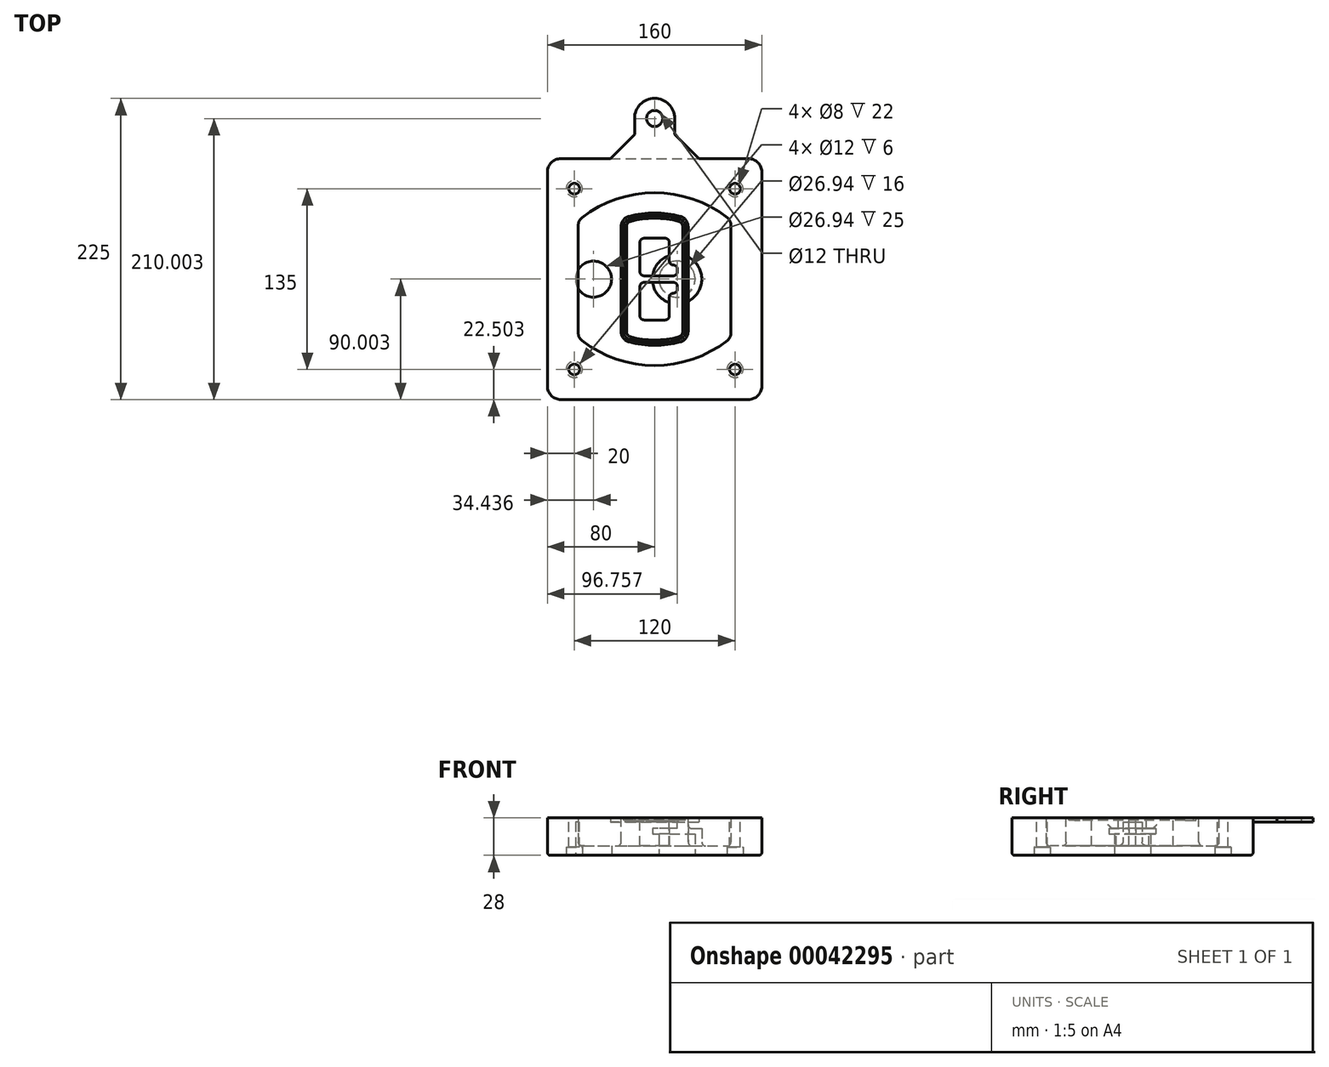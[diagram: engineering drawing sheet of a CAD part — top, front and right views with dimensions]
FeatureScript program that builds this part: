
annotation { "Feature Type Name" : "Feature", "Feature Type Description" : "" }
export const myFeature = defineFeature(function(context is Context, id is Id, definition is map)
    precondition{}
    {
        {
            var Q0;
            Q0=qCreatedBy(makeId("Top.planeOp"),FACE);
            var sketch = newSketch(context, id + "F0", { "sketchPlane" : qUnion([Q0])});
            skPoint(sketch, "E0.rect.middle", {"position": v(0, 0) * mm});
            skLineSegment(sketch, "E1.bottom", {"start": v(24.05, 28.38) * mm, "end": v(164.05, 28.38) * mm});
            skLineSegment(sketch, "E1.top", {"start": v(24.05, 208.38) * mm, "end": v(164.05, 208.38) * mm});
            skLineSegment(sketch, "E1.left", {"start": v(14.05, 38.38) * mm, "end": v(14.05, 198.38) * mm});
            skLineSegment(sketch, "E1.right", {"start": v(174.05, 38.38) * mm, "end": v(174.05, 198.38) * mm});
            skLineSegment(sketch, "E2", {"start": v(14.05, 208.38) * mm, "end": v(174.05, 28.38) * mm, "construction": true});
            skLineSegment(sketch, "E3", {"start": v(174.05, 208.38) * mm, "end": v(14.05, 28.38) * mm, "construction": true});
            skCircle(sketch, "E4", {"center": v(34.05, 185.88) * mm, "radius": 4 * mm});
            skCircle(sketch, "E5", {"center": v(154.05, 185.88) * mm, "radius": 4 * mm});
            skCircle(sketch, "E6", {"center": v(154.05, 50.88) * mm, "radius": 4 * mm});
            skCircle(sketch, "E7", {"center": v(34.05, 50.88) * mm, "radius": 4 * mm});
            skLineSegment(sketch, "E8", {"start": v(34.05, 185.88) * mm, "end": v(154.05, 185.88) * mm, "construction": true});
            skLineSegment(sketch, "E9", {"start": v(154.05, 185.88) * mm, "end": v(154.05, 50.88) * mm, "construction": true});
            skLineSegment(sketch, "E10", {"start": v(154.05, 50.88) * mm, "end": v(34.05, 50.88) * mm, "construction": true});
            skLineSegment(sketch, "E11", {"start": v(34.05, 50.88) * mm, "end": v(34.05, 185.88) * mm, "construction": true});
            skLineSegment(sketch, "E12", {"start": v(34.05, 158.68) * mm, "end": v(34.05, 78.09) * mm});
            skLineSegment(sketch, "E13", {"start": v(154.05, 158.68) * mm, "end": v(154.05, 78.09) * mm});
            skArc(sketch, "E14", {"start": v(150.2, 166.56) * mm, "mid": v(94.05, 185.88) * mm, "end": v(37.9, 166.56) * mm});
            skArc(sketch, "E15", {"start": v(37.9, 70.2) * mm, "mid": v(94.05, 50.88) * mm, "end": v(150.2, 70.2) * mm});
            skLineSegment(sketch, "E16", {"start": v(34.05, 118.38) * mm, "end": v(154.05, 118.38) * mm, "construction": true});
            skPoint(sketch, "E17.visualSharp", {"position": v(34.05, 73.38) * mm});
            skArc(sketch, "E17.filletArc", {"start": v(34.05, 78.09) * mm, "mid": v(35.06, 73.7) * mm, "end": v(37.9, 70.2) * mm});
            skPoint(sketch, "E18.visualSharp", {"position": v(34.05, 163.38) * mm});
            skArc(sketch, "E18.filletArc", {"start": v(37.9, 166.56) * mm, "mid": v(35.06, 163.06) * mm, "end": v(34.05, 158.68) * mm});
            skPoint(sketch, "E19.visualSharp", {"position": v(154.05, 163.38) * mm});
            skArc(sketch, "E19.filletArc", {"start": v(154.05, 158.68) * mm, "mid": v(153.04, 163.06) * mm, "end": v(150.2, 166.56) * mm});
            skPoint(sketch, "E20.visualSharp", {"position": v(154.05, 73.38) * mm});
            skArc(sketch, "E20.filletArc", {"start": v(150.2, 70.2) * mm, "mid": v(153.04, 73.7) * mm, "end": v(154.05, 78.09) * mm});
            skPoint(sketch, "E21.visualSharp", {"position": v(14.05, 208.38) * mm});
            skArc(sketch, "E21.filletArc", {"start": v(24.05, 208.38) * mm, "mid": v(16.98, 205.45) * mm, "end": v(14.05, 198.38) * mm});
            skPoint(sketch, "E22.visualSharp", {"position": v(174.05, 208.38) * mm});
            skArc(sketch, "E22.filletArc", {"start": v(174.05, 198.38) * mm, "mid": v(171.12, 205.45) * mm, "end": v(164.05, 208.38) * mm});
            skPoint(sketch, "E23.visualSharp", {"position": v(174.05, 28.38) * mm});
            skArc(sketch, "E23.filletArc", {"start": v(164.05, 28.38) * mm, "mid": v(171.12, 31.31) * mm, "end": v(174.05, 38.38) * mm});
            skPoint(sketch, "E24.visualSharp", {"position": v(14.05, 28.38) * mm});
            skArc(sketch, "E24.filletArc", {"start": v(14.05, 38.38) * mm, "mid": v(16.98, 31.31) * mm, "end": v(24.05, 28.38) * mm});
            skArc(sketch, "E25.0", {"start": v(151.05, 158.68) * mm, "mid": v(150.34, 161.75) * mm, "end": v(148.36, 164.2) * mm});
            skLineSegment(sketch, "E25.1", {"start": v(151.05, 158.68) * mm, "end": v(151.05, 78.09) * mm});
            skArc(sketch, "E25.2", {"start": v(148.36, 72.57) * mm, "mid": v(150.34, 75.02) * mm, "end": v(151.05, 78.09) * mm});
            skArc(sketch, "E25.3", {"start": v(39.74, 72.57) * mm, "mid": v(94.05, 53.88) * mm, "end": v(148.36, 72.57) * mm});
            skArc(sketch, "E25.4", {"start": v(37.05, 78.09) * mm, "mid": v(37.76, 75.02) * mm, "end": v(39.74, 72.57) * mm});
            skArc(sketch, "E25.5", {"start": v(148.36, 164.2) * mm, "mid": v(94.05, 182.88) * mm, "end": v(39.74, 164.2) * mm});
            skLineSegment(sketch, "E25.6", {"start": v(37.05, 158.68) * mm, "end": v(37.05, 78.09) * mm});
            skArc(sketch, "E25.7", {"start": v(39.74, 164.2) * mm, "mid": v(37.76, 161.75) * mm, "end": v(37.05, 158.68) * mm});
            skArc(sketch, "E26.0", {"start": v(35.43, 169.71) * mm, "mid": v(31.47, 164.82) * mm, "end": v(30.05, 158.68) * mm});
            skArc(sketch, "E26.1", {"start": v(152.67, 169.71) * mm, "mid": v(94.05, 189.88) * mm, "end": v(35.43, 169.71) * mm});
            skArc(sketch, "E26.2", {"start": v(158.05, 158.68) * mm, "mid": v(156.63, 164.82) * mm, "end": v(152.67, 169.71) * mm});
            skLineSegment(sketch, "E26.3", {"start": v(158.05, 158.68) * mm, "end": v(158.05, 78.09) * mm});
            skArc(sketch, "E26.4", {"start": v(152.67, 67.05) * mm, "mid": v(156.63, 71.95) * mm, "end": v(158.05, 78.09) * mm});
            skLineSegment(sketch, "E26.5", {"start": v(30.05, 158.68) * mm, "end": v(30.05, 78.09) * mm});
            skArc(sketch, "E26.6", {"start": v(35.43, 67.05) * mm, "mid": v(94.05, 46.88) * mm, "end": v(152.67, 67.05) * mm});
            skArc(sketch, "E26.7", {"start": v(30.05, 78.09) * mm, "mid": v(31.47, 71.95) * mm, "end": v(35.43, 67.05) * mm});
            skSolve(sketch);
        }
        {
            var Q0;
            Q0=makeQuery(id+"F0.imprint","IMPRINT",FACE,{"disambiguationData":[TD([[makeQuery(id+"F0.imprint","IMPRINT",EDGE,{"derivedFrom":sQuery(id+"F0.wireOp",EDGE,"E1.bottom")}),1.0]])]});
            var Q1;
            Q1=makeQuery(id+"F0.imprint","IMPRINT",FACE,{"disambiguationData":[TD([[makeQuery(id+"F0.imprint","IMPRINT",EDGE,{"derivedFrom":sQuery(id+"F0.wireOp",EDGE,"E12")}),1.0]])]});
            var Q2;
            Q2=makeQuery(id+"F0.imprint","IMPRINT",FACE,{"disambiguationData":[TD([[makeQuery(id+"F0.imprint","IMPRINT",EDGE,{"derivedFrom":sQuery(id+"F0.wireOp",EDGE,"E25.0")}),1.0]])]});
            var Q3;
            Q3=makeQuery(id+"F0.imprint","IMPRINT",FACE,{"disambiguationData":[TD([[makeQuery(id+"F0.imprint","IMPRINT",EDGE,{"derivedFrom":sQuery(id+"F0.wireOp",EDGE,"E12")}),-1.0]])]});
            extrude(context, id + "F1", {"entities" : qUnion([Q0, Q1, Q2, Q3]), "oppositeDirection" : true, "depth" : 25 * mm});
        }
        {
            var Q0;
            Q0=makeQuery(id+"F0.imprint","IMPRINT",FACE,{"disambiguationData":[TD([[makeQuery(id+"F0.imprint","IMPRINT",EDGE,{"derivedFrom":sQuery(id+"F0.wireOp",EDGE,"E12")}),1.0]])]});
            extrude(context, id + "F2", {"entities" : qUnion([Q0]), "operationType" : NewBodyOperationType.ADD, "depth" : 3 * mm});
        }
        {
            var Q0;
            Q0=makeQuery(id+"F0.imprint","IMPRINT",FACE,{"disambiguationData":[TD([[makeQuery(id+"F0.imprint","IMPRINT",EDGE,{"derivedFrom":sQuery(id+"F0.wireOp",EDGE,"E25.0")}),1.0]])]});
            extrude(context, id + "F3", {"entities" : qUnion([Q0]), "operationType" : NewBodyOperationType.REMOVE, "oppositeDirection" : true, "depth" : 18 * mm});
        }
        {
            var Q0;
            Q0=makeQuery(id+"F2.opExtrude","CAP_FACE",FACE,{"disambiguationData":[OSD([sQuery(id+"F0.wireOp",EDGE,"E12"),sQuery(id+"F0.wireOp",EDGE,"E13"),sQuery(id+"F0.wireOp",EDGE,"E14"),sQuery(id+"F0.wireOp",EDGE,"E15"),sQuery(id+"F0.wireOp",EDGE,"E17.filletArc"),sQuery(id+"F0.wireOp",EDGE,"E18.filletArc"),sQuery(id+"F0.wireOp",EDGE,"E19.filletArc"),sQuery(id+"F0.wireOp",EDGE,"E20.filletArc"),sQuery(id+"F0.wireOp",EDGE,"E25.0"),sQuery(id+"F0.wireOp",EDGE,"E25.1"),sQuery(id+"F0.wireOp",EDGE,"E25.2"),sQuery(id+"F0.wireOp",EDGE,"E25.3"),sQuery(id+"F0.wireOp",EDGE,"E25.4"),sQuery(id+"F0.wireOp",EDGE,"E25.5"),sQuery(id+"F0.wireOp",EDGE,"E25.6"),sQuery(id+"F0.wireOp",EDGE,"E25.7")])],"isStart":false});
            var sketch = newSketch(context, id + "F4", { "sketchPlane" : qUnion([Q0])});
            skArc(sketch, "E27.0", {"start": v(74.97, 71.41) * mm, "mid": v(94.05, 68.88) * mm, "end": v(113.13, 71.41) * mm});
            skArc(sketch, "E28.0", {"start": v(113.13, 165.35) * mm, "mid": v(94.05, 167.88) * mm, "end": v(74.97, 165.35) * mm});
            skLineSegment(sketch, "E29", {"start": v(69.05, 157.63) * mm, "end": v(69.05, 79.14) * mm});
            skLineSegment(sketch, "E30", {"start": v(119.05, 157.63) * mm, "end": v(119.05, 79.14) * mm});
            skLineSegment(sketch, "E31", {"start": v(69.05, 163.48) * mm, "end": v(119.05, 163.48) * mm, "construction": true});
            skLineSegment(sketch, "E32", {"start": v(69.05, 73.28) * mm, "end": v(119.05, 73.28) * mm, "construction": true});
            skPoint(sketch, "E33.visualSharp", {"position": v(69.05, 163.48) * mm});
            skArc(sketch, "E33.filletArc", {"start": v(74.97, 165.35) * mm, "mid": v(70.7, 162.5) * mm, "end": v(69.05, 157.63) * mm});
            skPoint(sketch, "E34.visualSharp", {"position": v(119.05, 163.48) * mm});
            skArc(sketch, "E34.filletArc", {"start": v(119.05, 157.63) * mm, "mid": v(117.4, 162.5) * mm, "end": v(113.13, 165.35) * mm});
            skPoint(sketch, "E35.visualSharp", {"position": v(119.05, 73.28) * mm});
            skArc(sketch, "E35.filletArc", {"start": v(113.13, 71.41) * mm, "mid": v(117.4, 74.27) * mm, "end": v(119.05, 79.14) * mm});
            skPoint(sketch, "E36.visualSharp", {"position": v(69.05, 73.28) * mm});
            skArc(sketch, "E36.filletArc", {"start": v(69.05, 79.14) * mm, "mid": v(70.7, 74.27) * mm, "end": v(74.97, 71.41) * mm});
            skArc(sketch, "E37.0", {"start": v(148.36, 164.2) * mm, "mid": v(94.05, 182.88) * mm, "end": v(39.74, 164.2) * mm});
            skArc(sketch, "E37.1", {"start": v(39.74, 164.2) * mm, "mid": v(37.76, 161.75) * mm, "end": v(37.05, 158.68) * mm});
            skLineSegment(sketch, "E37.2", {"start": v(37.05, 158.68) * mm, "end": v(37.05, 78.09) * mm});
            skArc(sketch, "E37.3", {"start": v(37.05, 78.09) * mm, "mid": v(37.76, 75.02) * mm, "end": v(39.74, 72.57) * mm});
            skArc(sketch, "E37.4", {"start": v(39.74, 72.57) * mm, "mid": v(94.05, 53.88) * mm, "end": v(148.36, 72.57) * mm});
            skArc(sketch, "E37.5", {"start": v(148.36, 72.57) * mm, "mid": v(150.34, 75.02) * mm, "end": v(151.05, 78.09) * mm});
            skLineSegment(sketch, "E37.6", {"start": v(151.05, 158.68) * mm, "end": v(151.05, 78.09) * mm});
            skArc(sketch, "E37.7", {"start": v(151.05, 158.68) * mm, "mid": v(150.34, 161.75) * mm, "end": v(148.36, 164.2) * mm});
            skLineSegment(sketch, "E38.0", {"start": v(117.05, 157.63) * mm, "end": v(117.05, 79.14) * mm});
            skArc(sketch, "E38.1", {"start": v(112.61, 73.34) * mm, "mid": v(115.81, 75.49) * mm, "end": v(117.05, 79.14) * mm});
            skArc(sketch, "E38.2", {"start": v(75.49, 73.34) * mm, "mid": v(94.05, 70.88) * mm, "end": v(112.61, 73.34) * mm});
            skArc(sketch, "E38.3", {"start": v(71.05, 79.14) * mm, "mid": v(72.29, 75.49) * mm, "end": v(75.49, 73.34) * mm});
            skLineSegment(sketch, "E38.4", {"start": v(71.05, 157.63) * mm, "end": v(71.05, 79.14) * mm});
            skArc(sketch, "E38.5", {"start": v(117.05, 157.63) * mm, "mid": v(115.81, 161.28) * mm, "end": v(112.61, 163.42) * mm});
            skArc(sketch, "E38.6", {"start": v(75.49, 163.42) * mm, "mid": v(72.29, 161.28) * mm, "end": v(71.05, 157.63) * mm});
            skArc(sketch, "E38.7", {"start": v(112.61, 163.42) * mm, "mid": v(94.05, 165.88) * mm, "end": v(75.49, 163.42) * mm});
            skArc(sketch, "E39.0", {"start": v(115.05, 157.63) * mm, "mid": v(114.23, 160.06) * mm, "end": v(112.1, 161.5) * mm});
            skLineSegment(sketch, "E39.1", {"start": v(115.05, 157.63) * mm, "end": v(115.05, 79.14) * mm});
            skArc(sketch, "E39.2", {"start": v(112.1, 75.27) * mm, "mid": v(114.23, 76.7) * mm, "end": v(115.05, 79.14) * mm});
            skArc(sketch, "E39.3", {"start": v(76, 75.27) * mm, "mid": v(94.05, 72.88) * mm, "end": v(112.1, 75.27) * mm});
            skArc(sketch, "E39.4", {"start": v(73.05, 79.14) * mm, "mid": v(73.87, 76.7) * mm, "end": v(76, 75.27) * mm});
            skArc(sketch, "E39.5", {"start": v(112.1, 161.5) * mm, "mid": v(94.05, 163.88) * mm, "end": v(76, 161.5) * mm});
            skLineSegment(sketch, "E39.6", {"start": v(73.05, 157.63) * mm, "end": v(73.05, 79.14) * mm});
            skArc(sketch, "E39.7", {"start": v(76, 161.5) * mm, "mid": v(73.87, 160.06) * mm, "end": v(73.05, 157.63) * mm});
            skLineSegment(sketch, "E40", {"start": v(69.05, 118.38) * mm, "end": v(119.05, 118.38) * mm, "construction": true});
            skLineSegment(sketch, "E41", {"start": v(83.05, 123.88) * mm, "end": v(83.05, 145.88) * mm});
            skLineSegment(sketch, "E42", {"start": v(86.05, 148.88) * mm, "end": v(102.05, 148.88) * mm});
            skLineSegment(sketch, "E43", {"start": v(105.05, 145.88) * mm, "end": v(105.05, 131.88) * mm});
            skLineSegment(sketch, "E44", {"start": v(108.05, 128.88) * mm, "end": v(108.05, 128.88) * mm});
            skLineSegment(sketch, "E45", {"start": v(111.05, 125.88) * mm, "end": v(111.05, 123.88) * mm});
            skLineSegment(sketch, "E46", {"start": v(108.05, 120.88) * mm, "end": v(86.05, 120.88) * mm});
            skPoint(sketch, "E47.visualSharp", {"position": v(83.05, 148.88) * mm});
            skArc(sketch, "E47.filletArc", {"start": v(86.05, 148.88) * mm, "mid": v(83.93, 148) * mm, "end": v(83.05, 145.88) * mm});
            skPoint(sketch, "E48.visualSharp", {"position": v(105.05, 148.88) * mm});
            skArc(sketch, "E48.filletArc", {"start": v(105.05, 145.88) * mm, "mid": v(104.17, 148) * mm, "end": v(102.05, 148.88) * mm});
            skPoint(sketch, "E49.visualSharp", {"position": v(105.05, 128.88) * mm});
            skArc(sketch, "E49.filletArc", {"start": v(105.05, 131.88) * mm, "mid": v(105.93, 129.76) * mm, "end": v(108.05, 128.88) * mm});
            skPoint(sketch, "E50.visualSharp", {"position": v(111.05, 128.88) * mm});
            skArc(sketch, "E50.filletArc", {"start": v(111.05, 125.88) * mm, "mid": v(110.17, 128) * mm, "end": v(108.05, 128.88) * mm});
            skPoint(sketch, "E51.visualSharp", {"position": v(111.05, 120.88) * mm});
            skArc(sketch, "E51.filletArc", {"start": v(108.05, 120.88) * mm, "mid": v(110.17, 121.76) * mm, "end": v(111.05, 123.88) * mm});
            skPoint(sketch, "E52.visualSharp", {"position": v(83.05, 120.88) * mm});
            skArc(sketch, "E52.filletArc", {"start": v(83.05, 123.88) * mm, "mid": v(83.93, 121.76) * mm, "end": v(86.05, 120.88) * mm});
            skLineSegment(sketch, "E53.0.MirrorCS", {"start": v(108.05, 115.88) * mm, "end": v(86.05, 115.88) * mm});
            skArc(sketch, "E54.0.MirrorCS", {"start": v(83.05, 112.88) * mm, "mid": v(83.93, 115) * mm, "end": v(86.05, 115.88) * mm});
            skLineSegment(sketch, "E55.0.MirrorCS", {"start": v(83.05, 112.88) * mm, "end": v(83.05, 90.88) * mm});
            skArc(sketch, "E56.0.MirrorCS", {"start": v(86.05, 87.88) * mm, "mid": v(83.93, 88.76) * mm, "end": v(83.05, 90.88) * mm});
            skLineSegment(sketch, "E57.0.MirrorCS", {"start": v(86.05, 87.88) * mm, "end": v(102.05, 87.88) * mm});
            skArc(sketch, "E58.0.MirrorCS", {"start": v(105.05, 90.88) * mm, "mid": v(104.17, 88.76) * mm, "end": v(102.05, 87.88) * mm});
            skLineSegment(sketch, "E59.0.MirrorCS", {"start": v(105.05, 90.88) * mm, "end": v(105.05, 104.88) * mm});
            skArc(sketch, "E60.0.MirrorCS", {"start": v(105.05, 104.88) * mm, "mid": v(105.93, 107) * mm, "end": v(108.05, 107.88) * mm});
            skArc(sketch, "E61.0.MirrorCS", {"start": v(111.05, 110.88) * mm, "mid": v(110.17, 108.76) * mm, "end": v(108.05, 107.88) * mm});
            skLineSegment(sketch, "E62.0.MirrorCS", {"start": v(111.05, 110.88) * mm, "end": v(111.05, 112.88) * mm});
            skArc(sketch, "E63.0.MirrorCS", {"start": v(108.05, 115.88) * mm, "mid": v(110.17, 115) * mm, "end": v(111.05, 112.88) * mm});
            skSolve(sketch);
        }
        {
            var Q0;
            Q0=makeQuery(id+"F4.imprint","IMPRINT",FACE,{"disambiguationData":[TD([[makeQuery(id+"F4.imprint","IMPRINT",EDGE,{"derivedFrom":sQuery(id+"F4.wireOp",EDGE,"E27.0")}),1.0]])]});
            var Q1;
            Q1=makeQuery(id+"F4.imprint","IMPRINT",FACE,{"disambiguationData":[TD([[makeQuery(id+"F4.imprint","IMPRINT",EDGE,{"derivedFrom":sQuery(id+"F4.wireOp",EDGE,"E38.0")}),-1.0]])]});
            var Q2;
            Q2=makeQuery(id+"F4.imprint","IMPRINT",FACE,{"disambiguationData":[TD([[makeQuery(id+"F4.imprint","IMPRINT",EDGE,{"derivedFrom":sQuery(id+"F4.wireOp",EDGE,"E39.0")}),1.0]])]});
            extrude(context, id + "F5", {"entities" : qUnion([Q0, Q1, Q2]), "operationType" : NewBodyOperationType.ADD, "endBound" : BoundingType.UP_TO_NEXT, "oppositeDirection" : true, "depth" : 25 * mm});
        }
        {
            var Q0;
            Q0=makeQuery(id+"F4.imprint","IMPRINT",FACE,{"disambiguationData":[TD([[makeQuery(id+"F4.imprint","IMPRINT",EDGE,{"derivedFrom":sQuery(id+"F4.wireOp",EDGE,"E38.0")}),-1.0]])]});
            extrude(context, id + "F6", {"entities" : qUnion([Q0]), "operationType" : NewBodyOperationType.REMOVE, "oppositeDirection" : true, "depth" : 2 * mm});
        }
        {
            var Q0;
            Q0=makeQuery(id+"F1.opExtrude","CAP_FACE",FACE,{"disambiguationData":[OSD([sQuery(id+"F0.wireOp",EDGE,"E1.bottom"),sQuery(id+"F0.wireOp",EDGE,"E1.top"),sQuery(id+"F0.wireOp",EDGE,"E1.left"),sQuery(id+"F0.wireOp",EDGE,"E1.right"),sQuery(id+"F0.wireOp",EDGE,"E4"),sQuery(id+"F0.wireOp",EDGE,"E5"),sQuery(id+"F0.wireOp",EDGE,"E6"),sQuery(id+"F0.wireOp",EDGE,"E7"),sQuery(id+"F0.wireOp",EDGE,"E21.filletArc"),sQuery(id+"F0.wireOp",EDGE,"E22.filletArc"),sQuery(id+"F0.wireOp",EDGE,"E23.filletArc"),sQuery(id+"F0.wireOp",EDGE,"E24.filletArc")])],"isStart":false});
            var sketch = newSketch(context, id + "F7", { "sketchPlane" : qUnion([Q0])});
            skCircle(sketch, "E64", {"center": v(110.8, -118.38) * mm, "radius": 13.47 * mm});
            skCircle(sketch, "E65", {"center": v(48.49, -118.38) * mm, "radius": 13.47 * mm});
            skLineSegment(sketch, "E66", {"start": v(174.05, -118.38) * mm, "end": v(14.05, -118.38) * mm});
            skCircle(sketch, "E67", {"center": v(110.8, -118.38) * mm, "radius": 18.47 * mm});
            skCircle(sketch, "E68", {"center": v(154.05, -185.88) * mm, "radius": 6 * mm});
            skCircle(sketch, "E69", {"center": v(34.05, -185.88) * mm, "radius": 6 * mm});
            skCircle(sketch, "E70", {"center": v(34.05, -50.88) * mm, "radius": 6 * mm});
            skCircle(sketch, "E71", {"center": v(154.05, -50.88) * mm, "radius": 6 * mm});
            skSolve(sketch);
        }
        {
            var Q0;
            {var subQ1=sQuery(id+"F7.wireOp",EDGE,"E66");var subQ4=sQuery(id+"F7.wireOp",EDGE,"E64");var subQ6=makeQuery(id+"F7.imprint","INTERSECT",VERTEX,{"disambiguationData":[OD(0.0)],"derivedFrom":[subQ4,subQ1]});Q0=makeQuery(id+"F7.imprint","IMPRINT",FACE,{"disambiguationData":[TD([[makeQuery(id+"F7.imprint","IMPRINT",EDGE,{"disambiguationData":[TD([[subQ6,-1.0]])],"derivedFrom":subQ4}),-1.0]])]});}
            var Q1;
            {var subQ0=sQuery(id+"F7.wireOp",EDGE,"E66");var subQ1=sQuery(id+"F7.wireOp",EDGE,"E64");var subQ3=makeQuery(id+"F7.imprint","INTERSECT",VERTEX,{"disambiguationData":[OD(0.0)],"derivedFrom":[subQ1,subQ0]});Q1=makeQuery(id+"F7.imprint","IMPRINT",FACE,{"disambiguationData":[TD([[makeQuery(id+"F7.imprint","IMPRINT",EDGE,{"disambiguationData":[TD([[subQ3,-1.0]])],"derivedFrom":subQ1}),1.0]])]});}
            var Q2;
            {var subQ0=sQuery(id+"F7.wireOp",EDGE,"E66");var subQ1=sQuery(id+"F7.wireOp",EDGE,"E64");var subQ3=makeQuery(id+"F7.imprint","INTERSECT",VERTEX,{"disambiguationData":[OD(0.0)],"derivedFrom":[subQ1,subQ0]});Q2=makeQuery(id+"F7.imprint","IMPRINT",FACE,{"disambiguationData":[TD([[makeQuery(id+"F7.imprint","IMPRINT",EDGE,{"disambiguationData":[TD([[subQ3,1.0]])],"derivedFrom":subQ1}),1.0]])]});}
            var Q3;
            {var subQ1=sQuery(id+"F7.wireOp",EDGE,"E66");var subQ4=sQuery(id+"F7.wireOp",EDGE,"E64");var subQ6=makeQuery(id+"F7.imprint","INTERSECT",VERTEX,{"disambiguationData":[OD(0.0)],"derivedFrom":[subQ4,subQ1]});Q3=makeQuery(id+"F7.imprint","IMPRINT",FACE,{"disambiguationData":[TD([[makeQuery(id+"F7.imprint","IMPRINT",EDGE,{"disambiguationData":[TD([[subQ6,1.0]])],"derivedFrom":subQ4}),-1.0]])]});}
            extrude(context, id + "F8", {"entities" : qUnion([Q0, Q1, Q2, Q3]), "operationType" : NewBodyOperationType.ADD, "oppositeDirection" : true, "depth" : 20 * mm});
        }
        {
            var Q0;
            {var subQ0=sQuery(id+"F7.wireOp",EDGE,"E66");var subQ1=sQuery(id+"F7.wireOp",EDGE,"E64");var subQ3=makeQuery(id+"F7.imprint","INTERSECT",VERTEX,{"disambiguationData":[OD(0.0)],"derivedFrom":[subQ1,subQ0]});Q0=makeQuery(id+"F7.imprint","IMPRINT",FACE,{"disambiguationData":[TD([[makeQuery(id+"F7.imprint","IMPRINT",EDGE,{"disambiguationData":[TD([[subQ3,-1.0]])],"derivedFrom":subQ1}),1.0]])]});}
            var Q1;
            {var subQ0=sQuery(id+"F7.wireOp",EDGE,"E66");var subQ1=sQuery(id+"F7.wireOp",EDGE,"E64");var subQ3=makeQuery(id+"F7.imprint","INTERSECT",VERTEX,{"disambiguationData":[OD(0.0)],"derivedFrom":[subQ1,subQ0]});Q1=makeQuery(id+"F7.imprint","IMPRINT",FACE,{"disambiguationData":[TD([[makeQuery(id+"F7.imprint","IMPRINT",EDGE,{"disambiguationData":[TD([[subQ3,1.0]])],"derivedFrom":subQ1}),1.0]])]});}
            extrude(context, id + "F9", {"entities" : qUnion([Q0, Q1]), "operationType" : NewBodyOperationType.REMOVE, "oppositeDirection" : true, "depth" : 16 * mm});
        }
        {
            var Q0;
            {var subQ0=sQuery(id+"F7.wireOp",EDGE,"E66");var subQ1=sQuery(id+"F7.wireOp",EDGE,"E65");var subQ3=makeQuery(id+"F7.imprint","INTERSECT",VERTEX,{"disambiguationData":[OD(0.0)],"derivedFrom":[subQ1,subQ0]});Q0=makeQuery(id+"F7.imprint","IMPRINT",FACE,{"disambiguationData":[TD([[makeQuery(id+"F7.imprint","IMPRINT",EDGE,{"disambiguationData":[TD([[subQ3,-1.0]])],"derivedFrom":subQ1}),1.0]])]});}
            var Q1;
            {var subQ0=sQuery(id+"F7.wireOp",EDGE,"E66");var subQ1=sQuery(id+"F7.wireOp",EDGE,"E65");var subQ3=makeQuery(id+"F7.imprint","INTERSECT",VERTEX,{"disambiguationData":[OD(0.0)],"derivedFrom":[subQ1,subQ0]});Q1=makeQuery(id+"F7.imprint","IMPRINT",FACE,{"disambiguationData":[TD([[makeQuery(id+"F7.imprint","IMPRINT",EDGE,{"disambiguationData":[TD([[subQ3,1.0]])],"derivedFrom":subQ1}),1.0]])]});}
            extrude(context, id + "F10", {"entities" : qUnion([Q0, Q1]), "operationType" : NewBodyOperationType.REMOVE, "oppositeDirection" : true, "depth" : 25 * mm});
        }
        {
            var Q0;
            Q0=makeQuery(id+"F7.imprint","IMPRINT",FACE,{"disambiguationData":[TD([[makeQuery(id+"F7.imprint","IMPRINT",EDGE,{"derivedFrom":sQuery(id+"F7.wireOp",EDGE,"E68")}),1.0]])]});
            var Q1;
            Q1=makeQuery(id+"F7.imprint","IMPRINT",FACE,{"disambiguationData":[TD([[makeQuery(id+"F7.imprint","IMPRINT",EDGE,{"derivedFrom":makeQuery(id+"F1.opExtrude","CAP_EDGE",EDGE,{"disambiguationData":[OSD([sQuery(id+"F0.wireOp",EDGE,"E5")])],"isStart":false})}),-1.0]])]});
            var Q2;
            Q2=makeQuery(id+"F7.imprint","IMPRINT",FACE,{"disambiguationData":[TD([[makeQuery(id+"F7.imprint","IMPRINT",EDGE,{"derivedFrom":sQuery(id+"F7.wireOp",EDGE,"E69")}),1.0]])]});
            var Q3;
            Q3=makeQuery(id+"F7.imprint","IMPRINT",FACE,{"disambiguationData":[TD([[makeQuery(id+"F7.imprint","IMPRINT",EDGE,{"derivedFrom":makeQuery(id+"F1.opExtrude","CAP_EDGE",EDGE,{"disambiguationData":[OSD([sQuery(id+"F0.wireOp",EDGE,"E4")])],"isStart":false})}),-1.0]])]});
            var Q4;
            Q4=makeQuery(id+"F7.imprint","IMPRINT",FACE,{"disambiguationData":[TD([[makeQuery(id+"F7.imprint","IMPRINT",EDGE,{"derivedFrom":sQuery(id+"F7.wireOp",EDGE,"E70")}),1.0]])]});
            var Q5;
            Q5=makeQuery(id+"F7.imprint","IMPRINT",FACE,{"disambiguationData":[TD([[makeQuery(id+"F7.imprint","IMPRINT",EDGE,{"derivedFrom":makeQuery(id+"F1.opExtrude","CAP_EDGE",EDGE,{"disambiguationData":[OSD([sQuery(id+"F0.wireOp",EDGE,"E7")])],"isStart":false})}),-1.0]])]});
            var Q6;
            Q6=makeQuery(id+"F7.imprint","IMPRINT",FACE,{"disambiguationData":[TD([[makeQuery(id+"F7.imprint","IMPRINT",EDGE,{"derivedFrom":sQuery(id+"F7.wireOp",EDGE,"E71")}),1.0]])]});
            var Q7;
            Q7=makeQuery(id+"F7.imprint","IMPRINT",FACE,{"disambiguationData":[TD([[makeQuery(id+"F7.imprint","IMPRINT",EDGE,{"derivedFrom":makeQuery(id+"F1.opExtrude","CAP_EDGE",EDGE,{"disambiguationData":[OSD([sQuery(id+"F0.wireOp",EDGE,"E6")])],"isStart":false})}),-1.0]])]});
            extrude(context, id + "F11", {"entities" : qUnion([Q0, Q1, Q2, Q3, Q4, Q5, Q6, Q7]), "operationType" : NewBodyOperationType.REMOVE, "oppositeDirection" : true, "depth" : 6 * mm});
        }
        {
            var Q0;
            Q0=makeQuery(id+"F9.boolean.opBoolean","COPY",FACE,{"derivedFrom":makeQuery(id+"F9.opExtrude","CAP_FACE",FACE,{"disambiguationData":[OSD([sQuery(id+"F7.wireOp",EDGE,"E64")])],"isStart":false})});
            var sketch = newSketch(context, id + "F12", { "sketchPlane" : qUnion([Q0])});
            skArc(sketch, "E72.0", {"start": v(105.05, -100.83) * mm, "mid": v(96.62, -106.56) * mm, "end": v(92.5, -115.88) * mm});
            skArc(sketch, "E72.1", {"start": v(92.5, -120.88) * mm, "mid": v(96.62, -130.2) * mm, "end": v(105.05, -135.93) * mm});
            skLineSegment(sketch, "E73", {"start": v(92.5, -120.88) * mm, "end": v(108.05, -120.88) * mm});
            skLineSegment(sketch, "E74.0", {"start": v(108.05, -115.88) * mm, "end": v(92.5, -115.88) * mm});
            skArc(sketch, "E74.1", {"start": v(108.05, -115.88) * mm, "mid": v(110.17, -115) * mm, "end": v(111.05, -112.88) * mm});
            skLineSegment(sketch, "E74.2", {"start": v(111.05, -110.88) * mm, "end": v(111.05, -112.88) * mm});
            skArc(sketch, "E74.3", {"start": v(111.05, -110.88) * mm, "mid": v(110.17, -108.76) * mm, "end": v(108.05, -107.88) * mm});
            skArc(sketch, "E74.4", {"start": v(105.05, -104.88) * mm, "mid": v(105.93, -107) * mm, "end": v(108.05, -107.88) * mm});
            skLineSegment(sketch, "E74.5", {"start": v(105.05, -100.83) * mm, "end": v(105.05, -104.88) * mm});
            skLineSegment(sketch, "E74.7", {"start": v(108.05, -120.88) * mm, "end": v(92.5, -120.88) * mm});
            skArc(sketch, "E74.8", {"start": v(108.05, -120.88) * mm, "mid": v(110.17, -121.76) * mm, "end": v(111.05, -123.88) * mm});
            skLineSegment(sketch, "E74.9", {"start": v(111.05, -125.88) * mm, "end": v(111.05, -123.88) * mm});
            skArc(sketch, "E74.10", {"start": v(111.05, -125.88) * mm, "mid": v(110.17, -128) * mm, "end": v(108.05, -128.88) * mm});
            skArc(sketch, "E74.11", {"start": v(105.05, -131.88) * mm, "mid": v(105.93, -129.76) * mm, "end": v(108.05, -128.88) * mm});
            skLineSegment(sketch, "E74.12", {"start": v(105.05, -135.93) * mm, "end": v(105.05, -131.88) * mm});
            skPoint(sketch, "E75.orphan", {"position": v(105.05, -145.88) * mm});
            skPoint(sketch, "E76.orphan", {"position": v(86.05, -120.88) * mm});
            skPoint(sketch, "E77.orphan", {"position": v(86.05, -115.88) * mm});
            skPoint(sketch, "E78.orphan", {"position": v(105.05, -90.88) * mm});
            skSolve(sketch);
        }
        {
            var Q0;
            {var subQ7=sQuery(id+"F12.wireOp",EDGE,"E72.0");var subQ14=sQuery(id+"F12.wireOp",EDGE,"E72.1");var subQ16=sQuery(id+"F12.wireOp",EDGE,"E74.1");var subQ18=sQuery(id+"F12.wireOp",EDGE,"E74.8");Q0=qUnion([makeQuery(id+"F12.imprint","IMPRINT",FACE,{"disambiguationData":[TD([[makeQuery(id+"F12.imprint","IMPRINT",EDGE,{"derivedFrom":subQ7}),1.0]])]}),makeQuery(id+"F12.imprint","IMPRINT",FACE,{"disambiguationData":[TD([[makeQuery(id+"F12.imprint","IMPRINT",EDGE,{"derivedFrom":subQ14}),1.0]])]}),makeQuery(id+"F12.imprint","IMPRINT",FACE,{"disambiguationData":[TD([[makeQuery(id+"F12.imprint","IMPRINT",EDGE,{"derivedFrom":subQ16}),1.0]])]}),makeQuery(id+"F12.imprint","IMPRINT",FACE,{"disambiguationData":[TD([[makeQuery(id+"F12.imprint","IMPRINT",EDGE,{"derivedFrom":subQ18}),-1.0]])]})]);}
            var Q1;
            Q1=makeQuery(id+"F5.boolean.opBoolean","SPLIT",FACE,{"disambiguationData":[TD([makeQuery(id+"F5.opExtrude","SWEPT_FACE",FACE,{"disambiguationData":[OSD([sQuery(id+"F4.wireOp",EDGE,"E41")])]})])],"derivedFrom":makeQuery(id+"F3.boolean.opBoolean","COPY",FACE,{"derivedFrom":makeQuery(id+"F3.opExtrude","CAP_FACE",FACE,{"disambiguationData":[OSD([sQuery(id+"F0.wireOp",EDGE,"E25.0"),sQuery(id+"F0.wireOp",EDGE,"E25.1"),sQuery(id+"F0.wireOp",EDGE,"E25.2"),sQuery(id+"F0.wireOp",EDGE,"E25.3"),sQuery(id+"F0.wireOp",EDGE,"E25.4"),sQuery(id+"F0.wireOp",EDGE,"E25.5"),sQuery(id+"F0.wireOp",EDGE,"E25.6"),sQuery(id+"F0.wireOp",EDGE,"E25.7")])],"isStart":false})})});
            extrude(context, id + "F13", {"entities" : qUnion([Q0]), "operationType" : NewBodyOperationType.REMOVE, "endBound" : BoundingType.UP_TO_SURFACE, "endBoundEntityFace" : qUnion([Q1]), "depth" : 25 * mm});
        }
        {
            var Q0;
            Q0=makeQuery(id+"F3.boolean.opBoolean","COPY",EDGE,{"derivedFrom":makeQuery(id+"F3.opExtrude","CAP_EDGE",EDGE,{"disambiguationData":[OSD([sQuery(id+"F0.wireOp",EDGE,"E25.6")])],"isStart":false})});
            var Q1;
            Q1=makeQuery(id+"F8.boolean.opBoolean","INTERSECT",EDGE,{"derivedFrom":[makeQuery(id+"F5.opExtrude","SWEPT_FACE",FACE,{"disambiguationData":[OSD([sQuery(id+"F4.wireOp",EDGE,"E30")])]}),makeQuery(id+"F8.opExtrude","CAP_FACE",FACE,{"disambiguationData":[OSD([sQuery(id+"F7.wireOp",EDGE,"E67")])],"isStart":false})]});
            var Q2;
            Q2=makeQuery(id+"F8.boolean.opBoolean","INTERSECT",EDGE,{"disambiguationData":[OD(1.0)],"derivedFrom":[makeQuery(id+"F5.opExtrude","SWEPT_FACE",FACE,{"disambiguationData":[OSD([sQuery(id+"F4.wireOp",EDGE,"E30")])]}),makeQuery(id+"F8.opExtrude","SWEPT_FACE",FACE,{"disambiguationData":[OSD([sQuery(id+"F7.wireOp",EDGE,"E67")])]})]});
            var Q3;
            {var subQ0=sQuery(id+"F4.wireOp",EDGE,"E30");Q3=makeQuery(id+"F8.boolean.opBoolean","SPLIT",EDGE,{"disambiguationData":[TD([makeQuery(id+"F5.opExtrude","SWEPT_FACE",FACE,{"disambiguationData":[OSD([sQuery(id+"F4.wireOp",EDGE,"E35.filletArc")])]})])],"derivedFrom":makeQuery(id+"F5.opExtrude","CAP_EDGE",EDGE,{"disambiguationData":[OSD([subQ0])],"isStart":false})});}
            var Q4;
            {var subQ0=sQuery(id+"F0.wireOp",EDGE,"E25.7");var subQ1=sQuery(id+"F0.wireOp",EDGE,"E25.1");var subQ2=sQuery(id+"F0.wireOp",EDGE,"E25.6");var subQ3=sQuery(id+"F0.wireOp",EDGE,"E25.5");var subQ4=sQuery(id+"F0.wireOp",EDGE,"E25.4");var subQ5=sQuery(id+"F0.wireOp",EDGE,"E25.0");var subQ6=sQuery(id+"F0.wireOp",EDGE,"E25.2");var subQ7=sQuery(id+"F0.wireOp",EDGE,"E25.3");Q4=makeQuery(id+"F8.boolean.opBoolean","INTERSECT",EDGE,{"derivedFrom":[makeQuery(id+"F5.boolean.opBoolean","SPLIT",FACE,{"disambiguationData":[TD([makeQuery(id+"F2.opExtrude","SWEPT_FACE",FACE,{"disambiguationData":[OSD([subQ5])]})])],"derivedFrom":makeQuery(id+"F3.boolean.opBoolean","COPY",FACE,{"derivedFrom":makeQuery(id+"F3.opExtrude","CAP_FACE",FACE,{"disambiguationData":[OSD([subQ5,subQ1,subQ6,subQ7,subQ4,subQ3,subQ2,subQ0])],"isStart":false})})}),makeQuery(id+"F8.opExtrude","SWEPT_FACE",FACE,{"disambiguationData":[OSD([sQuery(id+"F7.wireOp",EDGE,"E67")])]})]});}
            var Q5;
            Q5=makeQuery(id+"F8.boolean.opBoolean","INTERSECT",EDGE,{"disambiguationData":[OD(0.0)],"derivedFrom":[makeQuery(id+"F5.opExtrude","SWEPT_FACE",FACE,{"disambiguationData":[OSD([sQuery(id+"F4.wireOp",EDGE,"E30")])]}),makeQuery(id+"F8.opExtrude","SWEPT_FACE",FACE,{"disambiguationData":[OSD([sQuery(id+"F7.wireOp",EDGE,"E67")])]})]});
            fillet(context, id + "F14", {"entities" : qUnion([Q0, Q1, Q2, Q3, Q4, Q5]), "radius" : 3 * mm, "tangentPropagation" : true, "allowEdgeOverflow" : false});
        }
        {
            var Q0;
            Q0=makeQuery(id+"F1.opExtrude","CAP_EDGE",EDGE,{"disambiguationData":[OSD([sQuery(id+"F0.wireOp",EDGE,"E1.bottom")])],"isStart":false});
            fillet(context, id + "F15", {"entities" : qUnion([Q0]), "radius" : 2 * mm, "tangentPropagation" : true, "allowEdgeOverflow" : false});
        }
        {
            var Q0;
            {var subQ0=sQuery(id+"F0.wireOp",EDGE,"E1.bottom");var subQ1=sQuery(id+"F0.wireOp",EDGE,"E1.top");var subQ2=sQuery(id+"F0.wireOp",EDGE,"E1.left");var subQ3=sQuery(id+"F0.wireOp",EDGE,"E1.right");var subQ4=sQuery(id+"F0.wireOp",EDGE,"E4");var subQ5=sQuery(id+"F0.wireOp",EDGE,"E5");var subQ6=sQuery(id+"F0.wireOp",EDGE,"E6");var subQ7=sQuery(id+"F0.wireOp",EDGE,"E7");var subQ8=sQuery(id+"F0.wireOp",EDGE,"E21.filletArc");var subQ9=sQuery(id+"F0.wireOp",EDGE,"E22.filletArc");var subQ10=sQuery(id+"F0.wireOp",EDGE,"E23.filletArc");var subQ11=sQuery(id+"F0.wireOp",EDGE,"E24.filletArc");Q0=makeQuery(id+"F2.boolean.opBoolean","SPLIT",FACE,{"disambiguationData":[TD([makeQuery(id+"F1.opExtrude","SWEPT_FACE",FACE,{"disambiguationData":[OSD([subQ0])]})])],"derivedFrom":makeQuery(id+"F1.opExtrude","CAP_FACE",FACE,{"disambiguationData":[OSD([subQ0,subQ1,subQ2,subQ3,subQ4,subQ5,subQ6,subQ7,subQ8,subQ9,subQ10,subQ11])],"isStart":true})});}
            var sketch = newSketch(context, id + "F16", { "sketchPlane" : qUnion([Q0])});
            skLineSegment(sketch, "E79.0", {"start": v(24.05, 208.38) * mm, "end": v(164.05, 208.38) * mm});
            skArc(sketch, "E79.1", {"start": v(24.05, 208.38) * mm, "mid": v(16.98, 205.45) * mm, "end": v(14.05, 198.38) * mm});
            skLineSegment(sketch, "E79.2", {"start": v(14.05, 38.38) * mm, "end": v(14.05, 198.38) * mm});
            skArc(sketch, "E79.3", {"start": v(174.05, 198.38) * mm, "mid": v(171.12, 205.45) * mm, "end": v(164.05, 208.38) * mm});
            skLineSegment(sketch, "E79.4", {"start": v(174.05, 38.38) * mm, "end": v(174.05, 198.38) * mm});
            skArc(sketch, "E79.5", {"start": v(164.05, 28.38) * mm, "mid": v(171.12, 31.31) * mm, "end": v(174.05, 38.38) * mm});
            skLineSegment(sketch, "E79.6", {"start": v(24.05, 28.38) * mm, "end": v(164.05, 28.38) * mm});
            skCircle(sketch, "E79.7", {"center": v(34.05, 50.88) * mm, "radius": 4 * mm});
            skLineSegment(sketch, "E79.8", {"start": v(34.05, 158.68) * mm, "end": v(34.05, 78.09) * mm});
            skArc(sketch, "E79.9", {"start": v(150.2, 166.56) * mm, "mid": v(94.05, 185.88) * mm, "end": v(37.9, 166.56) * mm});
            skArc(sketch, "E79.10", {"start": v(37.9, 166.56) * mm, "mid": v(35.06, 163.06) * mm, "end": v(34.05, 158.68) * mm});
            skCircle(sketch, "E79.11", {"center": v(34.05, 185.88) * mm, "radius": 4 * mm});
            skCircle(sketch, "E79.12", {"center": v(154.05, 185.88) * mm, "radius": 4 * mm});
            skArc(sketch, "E79.13", {"start": v(154.05, 158.68) * mm, "mid": v(153.04, 163.06) * mm, "end": v(150.2, 166.56) * mm});
            skLineSegment(sketch, "E79.14", {"start": v(154.05, 158.68) * mm, "end": v(154.05, 78.09) * mm});
            skArc(sketch, "E79.15", {"start": v(150.2, 70.2) * mm, "mid": v(153.04, 73.7) * mm, "end": v(154.05, 78.09) * mm});
            skArc(sketch, "E79.16", {"start": v(37.9, 70.2) * mm, "mid": v(94.05, 50.88) * mm, "end": v(150.2, 70.2) * mm});
            skCircle(sketch, "E79.17", {"center": v(154.05, 50.88) * mm, "radius": 4 * mm});
            skArc(sketch, "E79.18", {"start": v(14.05, 38.38) * mm, "mid": v(16.98, 31.31) * mm, "end": v(24.05, 28.38) * mm});
            skLineSegment(sketch, "E80", {"start": v(94.05, 208.38) * mm, "end": v(94.05, 238.38) * mm, "construction": true});
            skCircle(sketch, "E81", {"center": v(94.05, 238.38) * mm, "radius": 6 * mm});
            skArc(sketch, "E82", {"start": v(109.05, 238.38) * mm, "mid": v(94.05, 253.38) * mm, "end": v(79.05, 238.38) * mm});
            skLineSegment(sketch, "E83", {"start": v(79.05, 238.38) * mm, "end": v(79.05, 226.38) * mm});
            skLineSegment(sketch, "E84", {"start": v(109.05, 238.38) * mm, "end": v(109.05, 226.38) * mm});
            skLineSegment(sketch, "E85", {"start": v(79.05, 226.38) * mm, "end": v(61.05, 208.38) * mm});
            skLineSegment(sketch, "E86", {"start": v(109.05, 226.38) * mm, "end": v(127.05, 208.38) * mm});
            skLineSegment(sketch, "E87", {"start": v(79.05, 226.38) * mm, "end": v(109.05, 226.38) * mm, "construction": true});
            skLineSegment(sketch, "E88", {"start": v(14.05, 118.38) * mm, "end": v(174.05, 118.38) * mm, "construction": true});
            skLineSegment(sketch, "E89.MirrorCS", {"start": v(79.05, 10.38) * mm, "end": v(109.05, 10.38) * mm, "construction": true});
            skCircle(sketch, "E90.MirrorC", {"center": v(94.05, -1.62) * mm, "radius": 6 * mm});
            skArc(sketch, "E91.MirrorCS", {"start": v(109.05, -1.62) * mm, "mid": v(94.05, -16.62) * mm, "end": v(79.05, -1.62) * mm});
            skLineSegment(sketch, "E92.MirrorCS", {"start": v(109.05, 10.38) * mm, "end": v(127.05, 28.38) * mm});
            skLineSegment(sketch, "E93.MirrorCS", {"start": v(79.05, -1.62) * mm, "end": v(79.05, 10.38) * mm});
            skLineSegment(sketch, "E94.MirrorCS", {"start": v(79.05, 10.38) * mm, "end": v(61.05, 28.38) * mm});
            skLineSegment(sketch, "E95.MirrorCS", {"start": v(109.05, -1.62) * mm, "end": v(109.05, 10.38) * mm});
            skLineSegment(sketch, "E96.MirrorCS", {"start": v(94.05, 28.38) * mm, "end": v(94.05, -1.62) * mm, "construction": true});
            skArc(sketch, "E97.MirrorCS", {"start": v(174.05, 38.38) * mm, "mid": v(171.12, 31.31) * mm, "end": v(164.05, 28.38) * mm});
            skSolve(sketch);
        }
        {
            var Q0;
            Q0=makeQuery(id+"F16.imprint","IMPRINT",FACE,{"disambiguationData":[TD([[makeQuery(id+"F16.imprint","IMPRINT",EDGE,{"derivedFrom":sQuery(id+"F16.wireOp",EDGE,"E81")}),-1.0]])]});
            var Q1;
            {var subQ4=sQuery(id+"F16.wireOp",EDGE,"E79.1");Q1=makeQuery(id+"F16.imprint","IMPRINT",FACE,{"disambiguationData":[TD([[makeQuery(id+"F16.imprint","IMPRINT",EDGE,{"derivedFrom":subQ4}),1.0]])]});}
            var Q2;
            Q2=makeQuery(id+"F16.imprint","IMPRINT",FACE,{"disambiguationData":[TD([[makeQuery(id+"F16.imprint","IMPRINT",EDGE,{"derivedFrom":sQuery(id+"F16.wireOp",EDGE,"E91.MirrorCS")}),-1.0]])]});
            var Q3;
            Q3=makeQuery(id+"F2.opExtrude","CAP_FACE",FACE,{"disambiguationData":[OSD([sQuery(id+"F0.wireOp",EDGE,"E12"),sQuery(id+"F0.wireOp",EDGE,"E13"),sQuery(id+"F0.wireOp",EDGE,"E14"),sQuery(id+"F0.wireOp",EDGE,"E15"),sQuery(id+"F0.wireOp",EDGE,"E17.filletArc"),sQuery(id+"F0.wireOp",EDGE,"E18.filletArc"),sQuery(id+"F0.wireOp",EDGE,"E19.filletArc"),sQuery(id+"F0.wireOp",EDGE,"E20.filletArc"),sQuery(id+"F0.wireOp",EDGE,"E25.0"),sQuery(id+"F0.wireOp",EDGE,"E25.1"),sQuery(id+"F0.wireOp",EDGE,"E25.2"),sQuery(id+"F0.wireOp",EDGE,"E25.3"),sQuery(id+"F0.wireOp",EDGE,"E25.4"),sQuery(id+"F0.wireOp",EDGE,"E25.5"),sQuery(id+"F0.wireOp",EDGE,"E25.6"),sQuery(id+"F0.wireOp",EDGE,"E25.7")])],"isStart":false});
            extrude(context, id + "F17", {"entities" : qUnion([Q0, Q1, Q2]), "operationType" : NewBodyOperationType.ADD, "endBound" : BoundingType.UP_TO_SURFACE, "endBoundEntityFace" : qUnion([Q3]), "depth" : 25 * mm});
        }
    });
